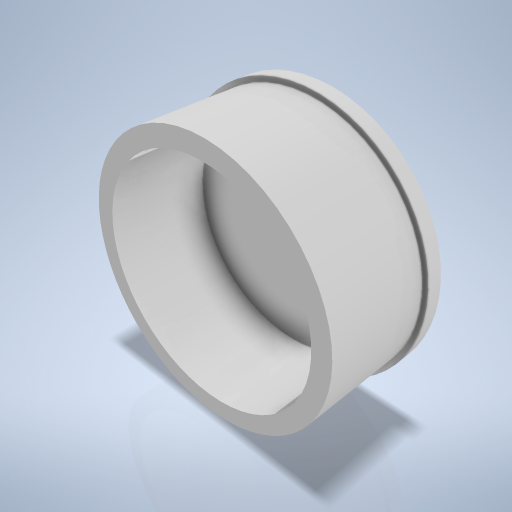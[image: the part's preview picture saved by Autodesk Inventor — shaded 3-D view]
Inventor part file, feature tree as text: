
AUTODESK INVENTOR PART (.ipt)
format: ipt  version: 2024.2 (Build 282272000, 272)  size: 260,608 bytes
history: native  units: mm
features: sketch x3, extrude x2, hole x1
ambient origin geometry x8: Origin, YZ Plane, XZ Plane, XY Plane, X Axis, Y Axis, Z Axis, Center Point
bodies: Volumenkörper1 (feature_tree)
feature tree (6):
  extrude  "Extrusion1"  Depth=9.5mm TaperAngle=0.0deg
  extrude  "Extrusion2"  Depth=1.5mm TaperAngle=0.0deg
  hole  "Bohrung1"  [1 undecoded]
  sketch  "Skizze1"  dims[d0=24.5mm d1=9.5mm d2=0.0mm]
  sketch  "Skizze2"  dims[d3=25.5mm d4=1.5mm d5=0.0mm]
  sketch  "Skizze3"  dims[d6=21.0mm d7=6.0mm d8=4.0mm d9=2.0mm d10=90.0deg d11=9.5mm d12=0.0mm]
note: 1 required parameter value undecoded (feature->parameter linkage not recoverable at this tier; creation-order binding heuristic only, values carry confidence <= 0.55)
